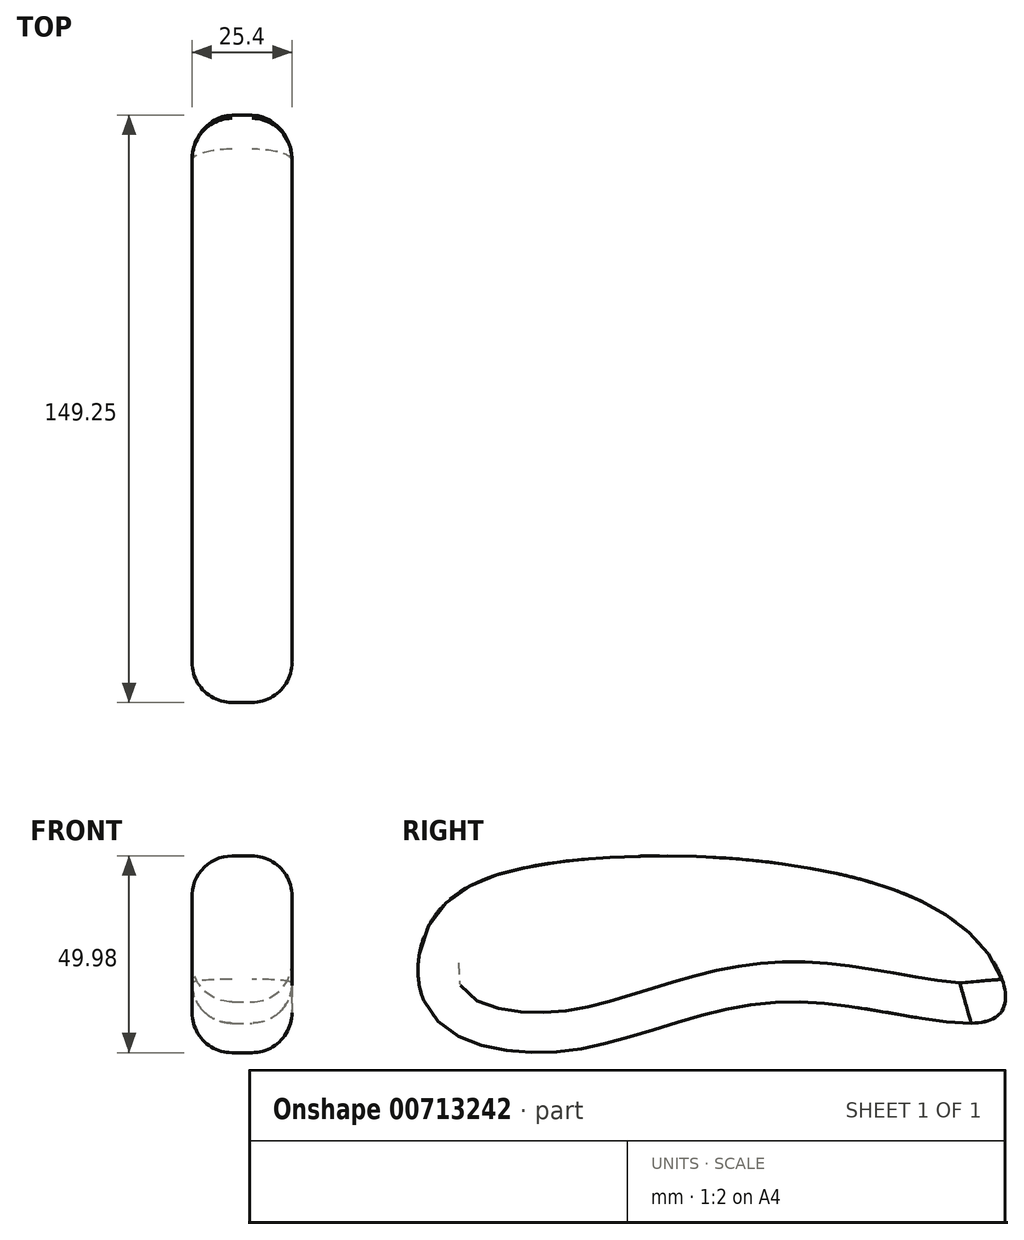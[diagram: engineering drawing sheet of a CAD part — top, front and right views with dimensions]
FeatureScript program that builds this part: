
annotation { "Feature Type Name" : "Feature", "Feature Type Description" : "" }
export const myFeature = defineFeature(function(context is Context, id is Id, definition is map)
    precondition{}
    {
        {
            var Q0;
            Q0=qCreatedBy(makeId("Right.planeOp"),FACE);
            var sketch = newSketch(context, id + "F0", { "sketchPlane" : qUnion([Q0])});
            skFitSpline(sketch, "E0", {"points": [v(-19.88, 38.92) * mm, v(-51.93, 23.26) * mm, v(-51.21, 0) * mm, v(-15.79, -8.8) * mm, v(40.6, 3.5) * mm, v(92.42, 0) * mm, v(81.34, 24.22) * mm, v(-19.88, 38.92) * mm]});
            skSolve(sketch);
        }
        {
            var Q0;
            Q0 = qSketchRegion(id + "F0", true);
            extrude(context, id + "F1", {"entities" : qUnion([Q0]), "depth" : 25.4 * mm, "offsetDistance" : 25.4 * mm});
        }
        {
            var Q0;
            Q0=makeQuery(id+"F1.opExtrude","CAP_EDGE",EDGE,{"disambiguationData":[OSD([sQuery(id+"F0.wireOp",EDGE,"E0")])],"isStart":false});
            var Q1;
            Q1=makeQuery(id+"F1.opExtrude","CAP_EDGE",EDGE,{"disambiguationData":[OSD([sQuery(id+"F0.wireOp",EDGE,"E0")])],"isStart":true});
            fillet(context, id + "F2", {"entities" : qUnion([Q0, Q1]), "radius" : 10.16 * mm, "tangentPropagation" : true, "allowEdgeOverflow" : false});
        }
    });
